# Revit family: WC-Care-Caroma Care Support Suite
name_source: partatom
category: Plumbing Fixtures
revit_build: Autodesk Revit Architecture 2012 (Build: 20110916_2132(x64)
units: mm (PartAtom-declared; Revit-internal decimal feet)

## types (2) — shared parameters
Assembly Code = C1030210
CW Connection = Yes
Description = Caravelle Care China Close Coupled 4.5/3L Support Suite
HW Connection = No
Hardware = Metal-Chrome-Caroma
Keynote = WC
Manufacturer = Caroma
Material_ANZRS = Porcelain-White-Caroma
PlumbingMaterial_ANZRS = Porcelain-White-Caroma
Vent Connection = No
WELSRating_ANZRS = 4
Waste Connection = Yes
zero-valued in all types: Default Elevation

## per-type parameters (varying)
| type | CWFU | Cost | Model | Type Comments | URL | WFU |
| S Trap | 2 | 0 $ |  | Caravelle Care 4.5/3L Support Toilet Suite | www.caroma.com.au | 3 |
| P Trap | 0 | 405.1 $ | W45001VP | Venecia 6/3L Smartflush Close Coupled Toilet Suite | www.stylus.com.au | 0 |

## geometry (parser evidence)
native form markers: Blend x4, Sweep x3
no freeform markers — native parametric forms only
